# Revit family: Sanitary_Taps-Mixers_AXOR_36707CHN-AXOR-ShowerSolutions-Thermostat22
name_source: partatom
category: Plumbing Fixtures
revit_build: Autodesk Revit 2018 (Build: 20170223_1515(x64)
units: mm (PartAtom-declared; Revit-internal decimal feet)

## family parameters
Always vertical = No
Cut with Voids When Loaded = No
OmniClass Number = 23.31.11.19.11
OmniClass Title = Thermostatically Controlled Faucet Mixing Valves
Part Type = Normal
Room Calculation Point = No
Round Connector Dimension = Use Diameter
Shared = No
Work Plane-Based = Yes

## types (4) — shared parameters
Always visible = Yes
BIMobject category = Taps & Mixers
Default Elevation = 1219.2 mm  [stored 4 ft]
Description = AXOR ShowerSolutions Thermostat for concealed installation softcube for 2 functions
Design country = Germany
EAN code = 4059625130698
Edition number = 1
GTIN code = https://4059625130698
IFC Classification = Valve
Installation instructions = https://www.axor-design.com
Manufacturer = AXOR
Manufacturer country = Germany
Manufacturer name = AXOR
Material 1 = AXOR - Plastic - Dark Gray
Model = 36707CHN
OmniClass Code = 23-31 11 19 11
OmniClass Description = Thermostatically Controlled Faucet Mixing Valves
Product Guid = 40b3170f-fda3-4bde-9ac0-4376039a7a14
Product SKU = 36707CHN
Product data url = https://www.bimobject.com
Product family = AXOR ShowerSolutions
Product group = Shower thermostat
Product name = 36707CHN AXOR ShowerSolutions Thermostat for concealed installation softcube for 2 functions
Product url = https://www.axor-design.com
QR code = https://www.bimobject.com
URL = https://www.axor-design.com
Uniclass 2015 Code = Pr_40_20_87_81
Uniclass 2015 Name = Shower thermostatic water supply sets
Weight Net (Kg) = 2

## per-type parameters (varying)
| type | Material 2 |
| 997 Polished Gold Optic | AXOR - Metal - 997 Polished Gold Optic |
| 677 Matt Black | AXOR - Metal - 677 Matt Black |
| 347 Brushed Black Chrome | AXOR - Metal - 347 Brushed Black Chrome |
| 007 Chrome | AXOR - Metal - 007 Chrome |

note: [stored X ft] marks values corroborated as IEEE doubles in the binary element streams (Revit-internal decimal feet)

## geometry (parser evidence)
native form markers: Sweep x3
no freeform markers — native parametric forms only
